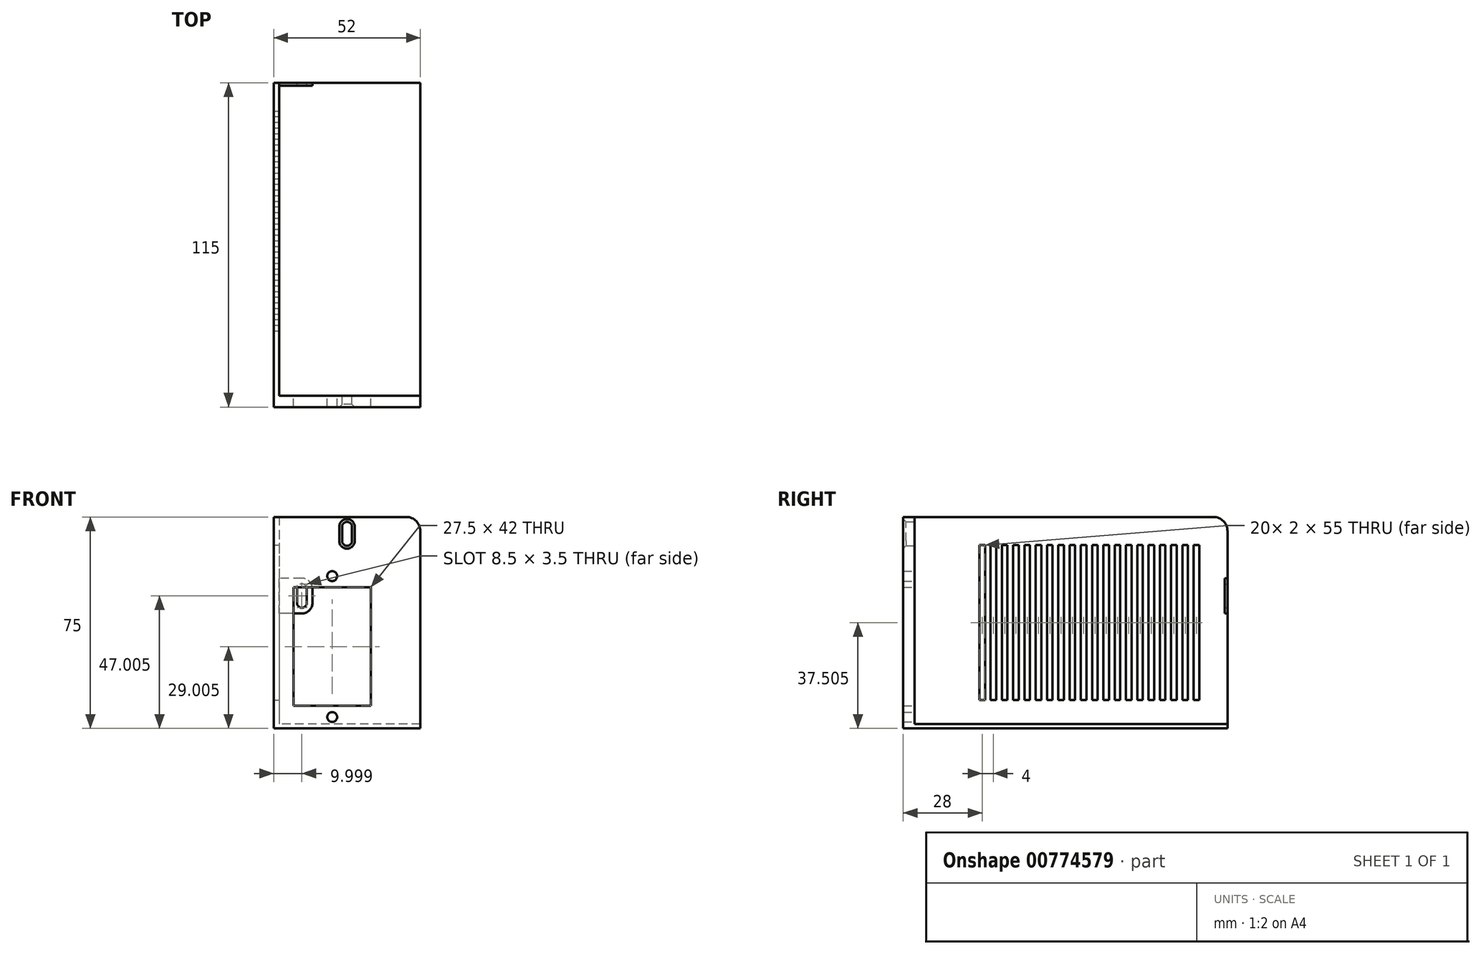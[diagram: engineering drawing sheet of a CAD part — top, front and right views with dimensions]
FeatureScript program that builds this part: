
annotation { "Feature Type Name" : "Feature", "Feature Type Description" : "" }
export const myFeature = defineFeature(function(context is Context, id is Id, definition is map)
    precondition{}
    {
        {
            var Q0;
            Q0=qCreatedBy(makeId("Front.planeOp"),FACE);
            var sketch = newSketch(context, id + "F0", { "sketchPlane" : qUnion([Q0])});
            skLineSegment(sketch, "E0.bottom", {"start": v(-72.92, 50.66) * mm, "end": v(-22.92, 50.66) * mm});
            skLineSegment(sketch, "E0.top", {"start": v(-72.92, -24.34) * mm, "end": v(-22.92, -24.34) * mm});
            skLineSegment(sketch, "E0.left", {"start": v(-72.92, 50.66) * mm, "end": v(-72.92, -24.34) * mm, "construction": true});
            skLineSegment(sketch, "E0.right", {"start": v(-22.92, 50.66) * mm, "end": v(-22.92, -24.34) * mm});
            skLineSegment(sketch, "E1.bottom", {"start": v(-67.92, 25.66) * mm, "end": v(-40.42, 25.66) * mm});
            skLineSegment(sketch, "E1.top", {"start": v(-67.92, -16.34) * mm, "end": v(-40.42, -16.34) * mm});
            skLineSegment(sketch, "E1.left", {"start": v(-67.92, 25.66) * mm, "end": v(-67.92, -16.34) * mm});
            skLineSegment(sketch, "E1.right", {"start": v(-40.42, 25.66) * mm, "end": v(-40.42, -16.34) * mm});
            skCircle(sketch, "E2", {"center": v(-54.17, 29.66) * mm, "radius": 1.75 * mm});
            skCircle(sketch, "E3", {"center": v(-54.17, -20.34) * mm, "radius": 1.75 * mm});
            skLineSegment(sketch, "E4", {"start": v(-54.17, 18.74) * mm, "end": v(-54.17, -11.65) * mm, "construction": true});
            skLineSegment(sketch, "E5", {"start": v(-72.32, 4.66) * mm, "end": v(-54.44, 4.66) * mm, "construction": true});
            skLineSegment(sketch, "E6", {"start": v(-72.92, 50.66) * mm, "end": v(-74.92, 50.66) * mm});
            skLineSegment(sketch, "E7", {"start": v(-74.92, 50.66) * mm, "end": v(-74.92, -24.34) * mm});
            skLineSegment(sketch, "E8", {"start": v(-74.92, -24.34) * mm, "end": v(-72.92, -24.34) * mm});
            skLineSegment(sketch, "E9", {"start": v(-48.92, 47.16) * mm, "end": v(-48.92, 42.16) * mm});
            skPoint(sketch, "E10", {"position": v(-48.92, 44.66) * mm});
            skArc(sketch, "E11.0.startCap", {"start": v(-50.67, 47.16) * mm, "mid": v(-48.92, 48.91) * mm, "end": v(-47.17, 47.16) * mm});
            skArc(sketch, "E11.0.endCap", {"start": v(-47.17, 42.16) * mm, "mid": v(-48.92, 40.41) * mm, "end": v(-50.67, 42.16) * mm});
            skLineSegment(sketch, "E11.0.left", {"start": v(-47.17, 47.16) * mm, "end": v(-47.17, 42.16) * mm});
            skLineSegment(sketch, "E11.0.right", {"start": v(-50.67, 47.16) * mm, "end": v(-50.67, 42.16) * mm});
            skSolve(sketch);
        }
        {
            var Q0;
            Q0 = qSketchRegion(id + "F0", true);
            extrude(context, id + "F1", {"entities" : qUnion([Q0]), "depth" : 4 * mm, "offsetDistance" : 25 * mm});
        }
        {
            var Q0;
            Q0=sQuery(id+"F0.wireOp",EDGE,"E0.left");
            cPlane(context, id + "F2", {"entities" : qUnion([Q0]), "cplaneType" : CPlaneType.LINE_ANGLE, "offset" : 25 * mm, "angle" : 0 * degree, "width" : 150 * mm, "height" : 150 * mm});
        }
        {
            var Q0;
            Q0=qCreatedBy(id+"F2.planeOp",FACE);
            var sketch = newSketch(context, id + "F3", { "sketchPlane" : qUnion([Q0])});
            skLineSegment(sketch, "E12.bottom", {"start": v(0, 50.66) * mm, "end": v(-111, 50.66) * mm});
            skLineSegment(sketch, "E12.top", {"start": v(0, -24.34) * mm, "end": v(-111, -24.34) * mm});
            skLineSegment(sketch, "E12.left", {"start": v(0, 50.66) * mm, "end": v(0, -24.34) * mm});
            skLineSegment(sketch, "E12.right", {"start": v(-111, 50.66) * mm, "end": v(-111, -24.34) * mm});
            skLineSegment(sketch, "E13", {"start": v(-111, -22.74) * mm, "end": v(0, -22.74) * mm});
            skLineSegment(sketch, "E14", {"start": v(-110, 50.66) * mm, "end": v(-110, -22.74) * mm});
            skLineSegment(sketch, "E15.bottom", {"start": v(-101, 40.66) * mm, "end": v(-99, 40.66) * mm});
            skLineSegment(sketch, "E15.top", {"start": v(-101, -14.34) * mm, "end": v(-99, -14.34) * mm});
            skLineSegment(sketch, "E15.left", {"start": v(-101, 40.66) * mm, "end": v(-101, -14.34) * mm});
            skLineSegment(sketch, "E15.right", {"start": v(-99, 40.66) * mm, "end": v(-99, -14.34) * mm});
            skLineSegment(sketch, "E16.1.0.0", {"start": v(-97, 40.66) * mm, "end": v(-97, -14.34) * mm});
            skLineSegment(sketch, "E16.1.0.1", {"start": v(-97, -14.34) * mm, "end": v(-95, -14.34) * mm});
            skLineSegment(sketch, "E16.1.0.2", {"start": v(-95, 40.66) * mm, "end": v(-95, -14.34) * mm});
            skLineSegment(sketch, "E16.1.0.3", {"start": v(-97, 40.66) * mm, "end": v(-95, 40.66) * mm});
            skLineSegment(sketch, "E16.2.0.0", {"start": v(-93, 40.66) * mm, "end": v(-93, -14.34) * mm});
            skLineSegment(sketch, "E16.2.0.1", {"start": v(-93, -14.34) * mm, "end": v(-91, -14.34) * mm});
            skLineSegment(sketch, "E16.2.0.2", {"start": v(-91, 40.66) * mm, "end": v(-91, -14.34) * mm});
            skLineSegment(sketch, "E16.2.0.3", {"start": v(-93, 40.66) * mm, "end": v(-91, 40.66) * mm});
            skLineSegment(sketch, "E16.3.0.0", {"start": v(-89, 40.66) * mm, "end": v(-89, -14.34) * mm});
            skLineSegment(sketch, "E16.3.0.1", {"start": v(-89, -14.34) * mm, "end": v(-87, -14.34) * mm});
            skLineSegment(sketch, "E16.3.0.2", {"start": v(-87, 40.66) * mm, "end": v(-87, -14.34) * mm});
            skLineSegment(sketch, "E16.3.0.3", {"start": v(-89, 40.66) * mm, "end": v(-87, 40.66) * mm});
            skLineSegment(sketch, "E16.4.0.0", {"start": v(-85, 40.66) * mm, "end": v(-85, -14.34) * mm});
            skLineSegment(sketch, "E16.4.0.1", {"start": v(-85, -14.34) * mm, "end": v(-83, -14.34) * mm});
            skLineSegment(sketch, "E16.4.0.2", {"start": v(-83, 40.66) * mm, "end": v(-83, -14.34) * mm});
            skLineSegment(sketch, "E16.4.0.3", {"start": v(-85, 40.66) * mm, "end": v(-83, 40.66) * mm});
            skLineSegment(sketch, "E16.5.0.0", {"start": v(-81, 40.66) * mm, "end": v(-81, -14.34) * mm});
            skLineSegment(sketch, "E16.5.0.1", {"start": v(-81, -14.34) * mm, "end": v(-79, -14.34) * mm});
            skLineSegment(sketch, "E16.5.0.2", {"start": v(-79, 40.66) * mm, "end": v(-79, -14.34) * mm});
            skLineSegment(sketch, "E16.5.0.3", {"start": v(-81, 40.66) * mm, "end": v(-79, 40.66) * mm});
            skLineSegment(sketch, "E16.6.0.0", {"start": v(-77, 40.66) * mm, "end": v(-77, -14.34) * mm});
            skLineSegment(sketch, "E16.6.0.1", {"start": v(-77, -14.34) * mm, "end": v(-75, -14.34) * mm});
            skLineSegment(sketch, "E16.6.0.2", {"start": v(-75, 40.66) * mm, "end": v(-75, -14.34) * mm});
            skLineSegment(sketch, "E16.6.0.3", {"start": v(-77, 40.66) * mm, "end": v(-75, 40.66) * mm});
            skLineSegment(sketch, "E16.7.0.0", {"start": v(-73, 40.66) * mm, "end": v(-73, -14.34) * mm});
            skLineSegment(sketch, "E16.7.0.1", {"start": v(-73, -14.34) * mm, "end": v(-71, -14.34) * mm});
            skLineSegment(sketch, "E16.7.0.2", {"start": v(-71, 40.66) * mm, "end": v(-71, -14.34) * mm});
            skLineSegment(sketch, "E16.7.0.3", {"start": v(-73, 40.66) * mm, "end": v(-71, 40.66) * mm});
            skLineSegment(sketch, "E16.8.0.0", {"start": v(-69, 40.66) * mm, "end": v(-69, -14.34) * mm});
            skLineSegment(sketch, "E16.8.0.1", {"start": v(-69, -14.34) * mm, "end": v(-67, -14.34) * mm});
            skLineSegment(sketch, "E16.8.0.2", {"start": v(-67, 40.66) * mm, "end": v(-67, -14.34) * mm});
            skLineSegment(sketch, "E16.8.0.3", {"start": v(-69, 40.66) * mm, "end": v(-67, 40.66) * mm});
            skLineSegment(sketch, "E16.9.0.0", {"start": v(-65, 40.66) * mm, "end": v(-65, -14.34) * mm});
            skLineSegment(sketch, "E16.9.0.1", {"start": v(-65, -14.34) * mm, "end": v(-63, -14.34) * mm});
            skLineSegment(sketch, "E16.9.0.2", {"start": v(-63, 40.66) * mm, "end": v(-63, -14.34) * mm});
            skLineSegment(sketch, "E16.9.0.3", {"start": v(-65, 40.66) * mm, "end": v(-63, 40.66) * mm});
            skLineSegment(sketch, "E16.10.0.0", {"start": v(-61, 40.66) * mm, "end": v(-61, -14.34) * mm});
            skLineSegment(sketch, "E16.10.0.1", {"start": v(-61, -14.34) * mm, "end": v(-59, -14.34) * mm});
            skLineSegment(sketch, "E16.10.0.2", {"start": v(-59, 40.66) * mm, "end": v(-59, -14.34) * mm});
            skLineSegment(sketch, "E16.10.0.3", {"start": v(-61, 40.66) * mm, "end": v(-59, 40.66) * mm});
            skLineSegment(sketch, "E16.11.0.0", {"start": v(-57, 40.66) * mm, "end": v(-57, -14.34) * mm});
            skLineSegment(sketch, "E16.11.0.1", {"start": v(-57, -14.34) * mm, "end": v(-55, -14.34) * mm});
            skLineSegment(sketch, "E16.11.0.2", {"start": v(-55, 40.66) * mm, "end": v(-55, -14.34) * mm});
            skLineSegment(sketch, "E16.11.0.3", {"start": v(-57, 40.66) * mm, "end": v(-55, 40.66) * mm});
            skLineSegment(sketch, "E16.12.0.0", {"start": v(-53, 40.66) * mm, "end": v(-53, -14.34) * mm});
            skLineSegment(sketch, "E16.12.0.1", {"start": v(-53, -14.34) * mm, "end": v(-51, -14.34) * mm});
            skLineSegment(sketch, "E16.12.0.2", {"start": v(-51, 40.66) * mm, "end": v(-51, -14.34) * mm});
            skLineSegment(sketch, "E16.12.0.3", {"start": v(-53, 40.66) * mm, "end": v(-51, 40.66) * mm});
            skLineSegment(sketch, "E16.13.0.0", {"start": v(-49, 40.66) * mm, "end": v(-49, -14.34) * mm});
            skLineSegment(sketch, "E16.13.0.1", {"start": v(-49, -14.34) * mm, "end": v(-47, -14.34) * mm});
            skLineSegment(sketch, "E16.13.0.2", {"start": v(-47, 40.66) * mm, "end": v(-47, -14.34) * mm});
            skLineSegment(sketch, "E16.13.0.3", {"start": v(-49, 40.66) * mm, "end": v(-47, 40.66) * mm});
            skLineSegment(sketch, "E16.14.0.0", {"start": v(-45, 40.66) * mm, "end": v(-45, -14.34) * mm});
            skLineSegment(sketch, "E16.14.0.1", {"start": v(-45, -14.34) * mm, "end": v(-43, -14.34) * mm});
            skLineSegment(sketch, "E16.14.0.2", {"start": v(-43, 40.66) * mm, "end": v(-43, -14.34) * mm});
            skLineSegment(sketch, "E16.14.0.3", {"start": v(-45, 40.66) * mm, "end": v(-43, 40.66) * mm});
            skLineSegment(sketch, "E16.15.0.0", {"start": v(-41, 40.66) * mm, "end": v(-41, -14.34) * mm});
            skLineSegment(sketch, "E16.15.0.1", {"start": v(-41, -14.34) * mm, "end": v(-39, -14.34) * mm});
            skLineSegment(sketch, "E16.15.0.2", {"start": v(-39, 40.66) * mm, "end": v(-39, -14.34) * mm});
            skLineSegment(sketch, "E16.15.0.3", {"start": v(-41, 40.66) * mm, "end": v(-39, 40.66) * mm});
            skLineSegment(sketch, "E16.16.0.0", {"start": v(-37, 40.66) * mm, "end": v(-37, -14.34) * mm});
            skLineSegment(sketch, "E16.16.0.1", {"start": v(-37, -14.34) * mm, "end": v(-35, -14.34) * mm});
            skLineSegment(sketch, "E16.16.0.2", {"start": v(-35, 40.66) * mm, "end": v(-35, -14.34) * mm});
            skLineSegment(sketch, "E16.16.0.3", {"start": v(-37, 40.66) * mm, "end": v(-35, 40.66) * mm});
            skLineSegment(sketch, "E16.17.0.0", {"start": v(-33, 40.66) * mm, "end": v(-33, -14.34) * mm});
            skLineSegment(sketch, "E16.17.0.1", {"start": v(-33, -14.34) * mm, "end": v(-31, -14.34) * mm});
            skLineSegment(sketch, "E16.17.0.2", {"start": v(-31, 40.66) * mm, "end": v(-31, -14.34) * mm});
            skLineSegment(sketch, "E16.17.0.3", {"start": v(-33, 40.66) * mm, "end": v(-31, 40.66) * mm});
            skLineSegment(sketch, "E16.18.0.0", {"start": v(-29, 40.66) * mm, "end": v(-29, -14.34) * mm});
            skLineSegment(sketch, "E16.18.0.1", {"start": v(-29, -14.34) * mm, "end": v(-27, -14.34) * mm});
            skLineSegment(sketch, "E16.18.0.2", {"start": v(-27, 40.66) * mm, "end": v(-27, -14.34) * mm});
            skLineSegment(sketch, "E16.18.0.3", {"start": v(-29, 40.66) * mm, "end": v(-27, 40.66) * mm});
            skLineSegment(sketch, "E16.19.0.0", {"start": v(-25, 40.66) * mm, "end": v(-25, -14.34) * mm});
            skLineSegment(sketch, "E16.19.0.1", {"start": v(-25, -14.34) * mm, "end": v(-23, -14.34) * mm});
            skLineSegment(sketch, "E16.19.0.2", {"start": v(-23, 40.66) * mm, "end": v(-23, -14.34) * mm});
            skLineSegment(sketch, "E16.19.0.3", {"start": v(-25, 40.66) * mm, "end": v(-23, 40.66) * mm});
            skLineSegment(sketch, "E16.direction1", {"start": v(-101, -14.34) * mm, "end": v(-97, -14.34) * mm, "construction": true});
            skSolve(sketch);
        }
        {
            var Q0;
            Q0=makeQuery(id+"F3.imprint","IMPRINT",FACE,{"disambiguationData":[TD([[makeQuery(id+"F3.imprint","IMPRINT",EDGE,{"derivedFrom":sQuery(id+"F3.wireOp",EDGE,"E12.bottom")}),1.0]])]});
            var Q1;
            {var subQ0=sQuery(id+"F3.wireOp",EDGE,"E12.top");Q1=makeQuery(id+"F3.imprint","IMPRINT",FACE,{"disambiguationData":[TD([[makeQuery(id+"F3.imprint","IMPRINT",EDGE,{"derivedFrom":subQ0}),-1.0]])]});}
            var Q2;
            {var subQ3=sQuery(id+"F3.wireOp",EDGE,"E14");Q2=makeQuery(id+"F3.imprint","IMPRINT",FACE,{"disambiguationData":[TD([[makeQuery(id+"F3.imprint","IMPRINT",EDGE,{"derivedFrom":subQ3}),1.0]])]});}
            var Q3;
            Q3=sQuery(id+"F0.wireOp",VERTEX,"E6.end");
            extrude(context, id + "F4", {"entities" : qUnion([Q0, Q1, Q2]), "operationType" : NewBodyOperationType.ADD, "endBound" : BoundingType.UP_TO_VERTEX, "depth" : 25 * mm, "endBoundEntityVertex" : qUnion([Q3]), "offsetDistance" : 25 * mm});
        }
        {
            var Q0;
            Q0=makeQuery(id+"F1.opExtrude","CAP_EDGE",EDGE,{"disambiguationData":[OSD([sQuery(id+"F0.wireOp",EDGE,"J2TVenfy-H0t2-NaJU-XWoU-IOxrSv4zuDt0")])],"isStart":false});
            var Q1;
            Q1=makeQuery(id+"F1.opExtrude","CAP_EDGE",EDGE,{"disambiguationData":[OSD([sQuery(id+"F0.wireOp",EDGE,"E11.0.left")])],"isStart":false});
            chamfer(context, id + "F5", {"entities" : qUnion([Q0, Q1]), "width" : 1 * mm, "tangentPropagation" : true});
        }
        {
            var Q0;
            {var subQ0=sQuery(id+"F3.wireOp",EDGE,"E12.top");Q0=makeQuery(id+"F3.imprint","IMPRINT",FACE,{"disambiguationData":[TD([[makeQuery(id+"F3.imprint","IMPRINT",EDGE,{"derivedFrom":subQ0}),-1.0]])]});}
            var Q1;
            Q1=sQuery(id+"F0.wireOp",VERTEX,"E0.top.end");
            extrude(context, id + "F6", {"entities" : qUnion([Q0]), "operationType" : NewBodyOperationType.ADD, "endBound" : BoundingType.UP_TO_VERTEX, "oppositeDirection" : true, "depth" : 25 * mm, "endBoundEntityVertex" : qUnion([Q1]), "offsetDistance" : 25 * mm});
        }
        {
            var Q0;
            Q0=sQuery(id+"F3.wireOp",EDGE,"E12.right");
            cPlane(context, id + "F7", {"entities" : qUnion([Q0]), "cplaneType" : CPlaneType.LINE_ANGLE, "offset" : 25 * mm, "angle" : 90 * degree, "width" : 150 * mm, "height" : 150 * mm});
        }
        {
            var Q0;
            Q0=qCreatedBy(id+"F7.planeOp",FACE);
            var sketch = newSketch(context, id + "F8", { "sketchPlane" : qUnion([Q0])});
            skLineSegment(sketch, "E17.right", {"start": v(72.92, 16.41) * mm, "end": v(72.92, 28.91) * mm});
            skLineSegment(sketch, "E18", {"start": v(64.92, 25.16) * mm, "end": v(64.92, 20.16) * mm});
            skPoint(sketch, "E19", {"position": v(64.92, 22.66) * mm});
            skArc(sketch, "E20.0.startCap", {"start": v(63.17, 25.16) * mm, "mid": v(64.92, 26.91) * mm, "end": v(66.67, 25.16) * mm});
            skArc(sketch, "E20.0.endCap", {"start": v(66.67, 20.16) * mm, "mid": v(64.92, 18.41) * mm, "end": v(63.17, 20.16) * mm});
            skLineSegment(sketch, "E20.0.left", {"start": v(66.67, 25.16) * mm, "end": v(66.67, 20.16) * mm});
            skLineSegment(sketch, "E20.0.right", {"start": v(63.17, 25.16) * mm, "end": v(63.17, 20.16) * mm});
            skLineSegment(sketch, "E21", {"start": v(61.17, 25.16) * mm, "end": v(61.17, 20.16) * mm});
            skArc(sketch, "E22", {"start": v(61.17, 20.16) * mm, "mid": v(62.27, 17.51) * mm, "end": v(64.92, 16.41) * mm});
            skArc(sketch, "E23", {"start": v(61.17, 25.16) * mm, "mid": v(62.27, 27.82) * mm, "end": v(64.92, 28.91) * mm});
            skLineSegment(sketch, "E24", {"start": v(64.92, 28.91) * mm, "end": v(72.92, 28.91) * mm});
            skLineSegment(sketch, "E25", {"start": v(64.92, 16.41) * mm, "end": v(72.92, 16.41) * mm});
            skSolve(sketch);
        }
        {
            var Q0;
            Q0=makeQuery(id+"F8.imprint","IMPRINT",FACE,{"disambiguationData":[TD([[makeQuery(id+"F8.imprint","IMPRINT",EDGE,{"derivedFrom":sQuery(id+"F8.wireOp",EDGE,"E17.right")}),1.0]])]});
            var Q1;
            Q1=sQuery(id+"F3.wireOp",VERTEX,"E14.start");
            extrude(context, id + "F9", {"entities" : qUnion([Q0]), "operationType" : NewBodyOperationType.ADD, "endBound" : BoundingType.UP_TO_VERTEX, "oppositeDirection" : true, "depth" : 25 * mm, "endBoundEntityVertex" : qUnion([Q1]), "offsetDistance" : 25 * mm});
        }
        {
            var Q0;
            Q0=makeQuery(id+"F1.opExtrude","SWEPT_EDGE",EDGE,{"disambiguationData":[OSD([sQuery(id+"F0.wireOp",EDGE,"E0.bottom"),sQuery(id+"F0.wireOp",EDGE,"E0.right")])]});
            var Q1;
            Q1=makeQuery(id+"F4.opExtrude","SWEPT_EDGE",EDGE,{"disambiguationData":[OSD([sQuery(id+"F3.wireOp",EDGE,"E12.bottom"),sQuery(id+"F3.wireOp",EDGE,"E12.right")])]});
            fillet(context, id + "F10", {"entities" : qUnion([Q0, Q1]), "radius" : 5 * mm, "tangentPropagation" : true, "allowEdgeOverflow" : false});
        }
    });
